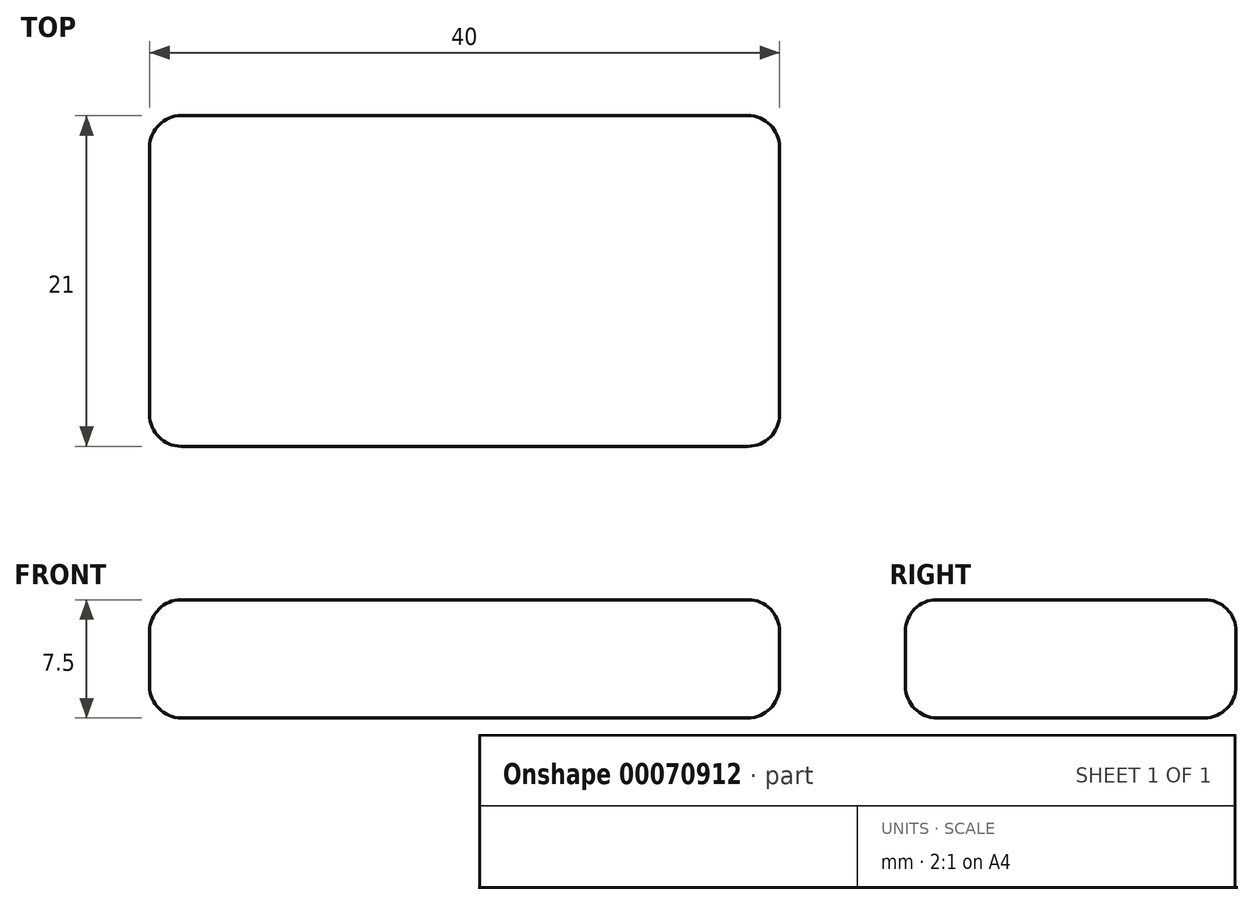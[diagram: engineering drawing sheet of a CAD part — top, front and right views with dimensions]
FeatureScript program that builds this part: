
annotation { "Feature Type Name" : "Feature", "Feature Type Description" : "" }
export const myFeature = defineFeature(function(context is Context, id is Id, definition is map)
    precondition{}
    {
        {
            var Q0;
            Q0=qCreatedBy(makeId("Top.planeOp"),FACE);
            var sketch = newSketch(context, id + "F0", { "sketchPlane" : qUnion([Q0])});
            skLineSegment(sketch, "E0.rect.bottom", {"start": v(20, -10.5) * mm, "end": v(-20, -10.5) * mm});
            skLineSegment(sketch, "E0.rect.top", {"start": v(20, 10.5) * mm, "end": v(-20, 10.5) * mm});
            skLineSegment(sketch, "E0.rect.left", {"start": v(20, -10.5) * mm, "end": v(20, 10.5) * mm});
            skLineSegment(sketch, "E0.rect.right", {"start": v(-20, -10.5) * mm, "end": v(-20, 10.5) * mm});
            skPoint(sketch, "E0.rect.middle", {"position": v(0, 0) * mm});
            skSolve(sketch);
        }
        {
            var Q0;
            Q0=makeQuery(id+"F0.imprint","IMPRINT",FACE,{"disambiguationData":[TD([[makeQuery(id+"F0.imprint","IMPRINT",EDGE,{"derivedFrom":sQuery(id+"F0.wireOp",EDGE,"E0.rect.bottom")}),-1.0]])]});
            extrude(context, id + "F1", {"entities" : qUnion([Q0]), "depth" : 7.5 * mm});
        }
        {
            var Q0;
            Q0=makeQuery(id+"F1.opExtrude","CAP_FACE",FACE,{"disambiguationData":[OSD([sQuery(id+"F0.wireOp",EDGE,"E0.rect.bottom"),sQuery(id+"F0.wireOp",EDGE,"E0.rect.top"),sQuery(id+"F0.wireOp",EDGE,"E0.rect.left"),sQuery(id+"F0.wireOp",EDGE,"E0.rect.right")])],"isStart":false});
            var Q1;
            Q1=makeQuery(id+"F1.opExtrude","CAP_FACE",FACE,{"disambiguationData":[OSD([sQuery(id+"F0.wireOp",EDGE,"E0.rect.bottom"),sQuery(id+"F0.wireOp",EDGE,"E0.rect.top"),sQuery(id+"F0.wireOp",EDGE,"E0.rect.left"),sQuery(id+"F0.wireOp",EDGE,"E0.rect.right")])],"isStart":true});
            var Q2;
            Q2=makeQuery(id+"F1.opExtrude","SWEPT_FACE",FACE,{"disambiguationData":[OSD([sQuery(id+"F0.wireOp",EDGE,"E0.rect.bottom")])]});
            var Q3;
            Q3=makeQuery(id+"F1.opExtrude","SWEPT_FACE",FACE,{"disambiguationData":[OSD([sQuery(id+"F0.wireOp",EDGE,"E0.rect.top")])]});
            fillet(context, id + "F2", {"entities" : qUnion([Q0, Q1, Q2, Q3]), "radius" : 2 * mm, "tangentPropagation" : true, "allowEdgeOverflow" : false});
        }
    });
